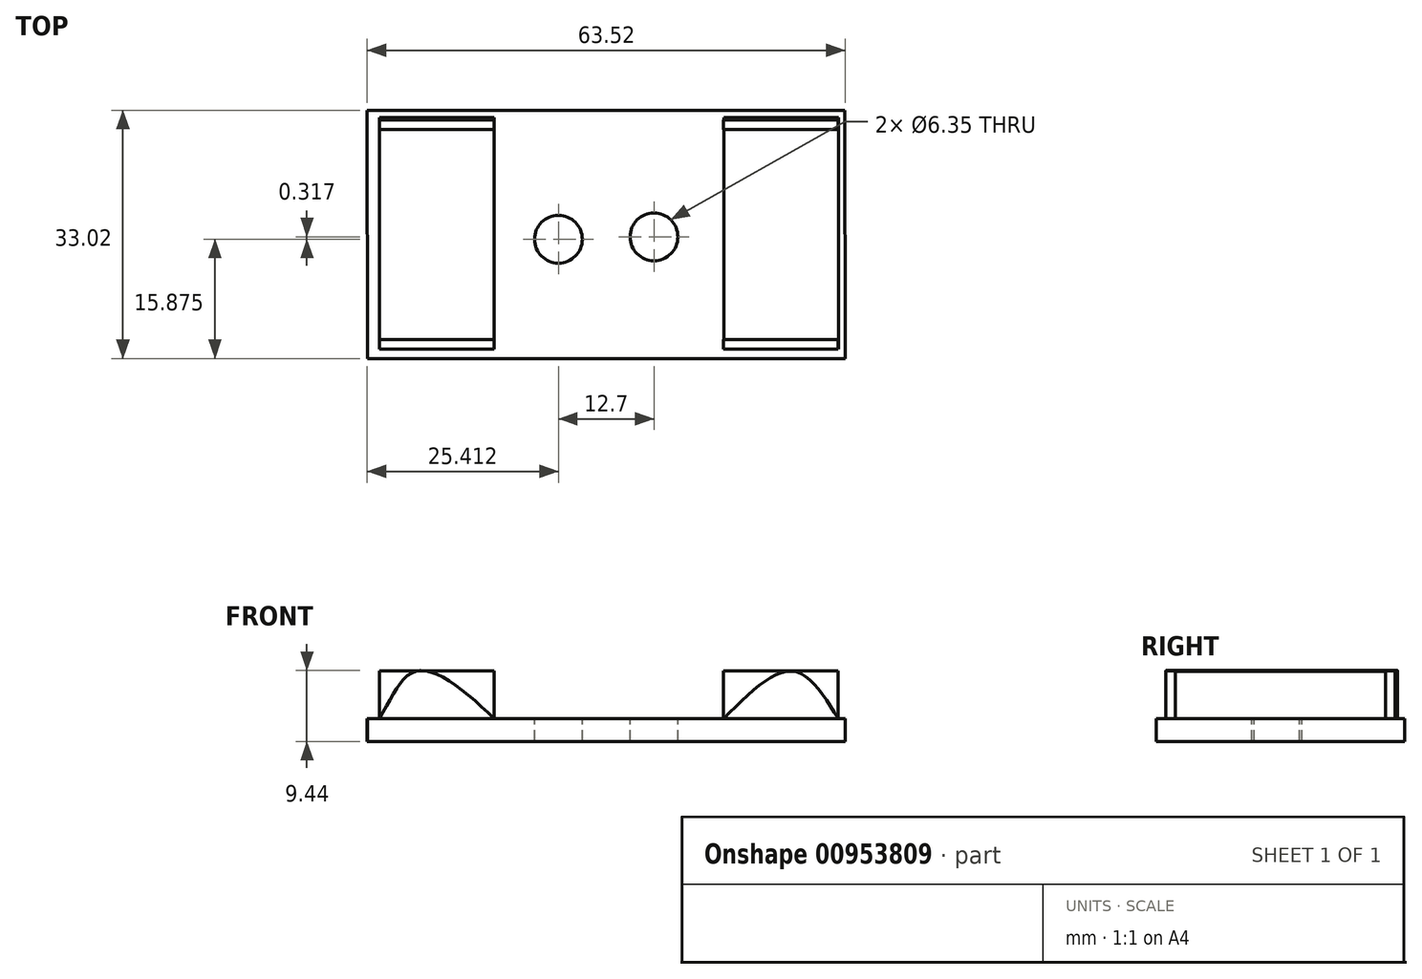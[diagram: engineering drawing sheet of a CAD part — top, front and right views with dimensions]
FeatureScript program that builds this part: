
annotation { "Feature Type Name" : "Feature", "Feature Type Description" : "" }
export const myFeature = defineFeature(function(context is Context, id is Id, definition is map)
    precondition{}
    {
        {
            var Q0;
            Q0=qCreatedBy(makeId("Top.planeOp"),FACE);
            var sketch = newSketch(context, id + "F0", { "sketchPlane" : qUnion([Q0])});
            skLineSegment(sketch, "E0", {"start": v(-16.83, 0) * mm, "end": v(46.67, 0) * mm});
            skLineSegment(sketch, "E1", {"start": v(46.67, 0) * mm, "end": v(46.65, 33.02) * mm});
            skLineSegment(sketch, "E2", {"start": v(46.65, 33.02) * mm, "end": v(-16.85, 33.02) * mm});
            skLineSegment(sketch, "E3", {"start": v(-16.85, 33.02) * mm, "end": v(-16.83, 0) * mm});
            skSolve(sketch);
        }
        {
            var Q0;
            Q0 = qSketchRegion(id + "F0", true);
            extrude(context, id + "F1", {"entities" : qUnion([Q0]), "depth" : 3.05 * mm, "offsetDistance" : 25.4 * mm});
        }
        {
            var Q0;
            Q0=makeQuery(id+"F1.opExtrude","CAP_FACE",FACE,{"disambiguationData":[OSD([sQuery(id+"F0.wireOp",EDGE,"E0"),sQuery(id+"F0.wireOp",EDGE,"E1"),sQuery(id+"F0.wireOp",EDGE,"E2"),sQuery(id+"F0.wireOp",EDGE,"E3")])],"isStart":false});
            var sketch = newSketch(context, id + "F2", { "sketchPlane" : qUnion([Q0])});
            skCircle(sketch, "E4", {"center": v(8.56, 15.88) * mm, "radius": 3.18 * mm});
            skCircle(sketch, "E5", {"center": v(21.26, 16.2) * mm, "radius": 3.18 * mm});
            skPoint(sketch, "E5.centerSnap0", {"position": v(-16.2, 16.2) * mm});
            skSolve(sketch);
        }
        {
            var Q0;
            Q0 = qSketchRegion(id + "F2", true);
            extrude(context, id + "F3", {"entities" : qUnion([Q0]), "operationType" : NewBodyOperationType.REMOVE, "endBound" : BoundingType.UP_TO_NEXT, "oppositeDirection" : true, "depth" : 3.05 * mm, "offsetDistance" : 25.4 * mm});
        }
        {
            var Q0;
            Q0=makeQuery(id+"F1.opExtrude","CAP_FACE",FACE,{"disambiguationData":[OSD([sQuery(id+"F0.wireOp",EDGE,"E0"),sQuery(id+"F0.wireOp",EDGE,"E1"),sQuery(id+"F0.wireOp",EDGE,"E2"),sQuery(id+"F0.wireOp",EDGE,"E3")])],"isStart":false});
            var sketch = newSketch(context, id + "F4", { "sketchPlane" : qUnion([Q0])});
            skLineSegment(sketch, "E6.bottom", {"start": v(-15.24, 31.75) * mm, "end": v(0, 31.75) * mm});
            skLineSegment(sketch, "E6.top", {"start": v(-15.24, 1.27) * mm, "end": v(0, 1.27) * mm});
            skLineSegment(sketch, "E6.left", {"start": v(-15.24, 31.75) * mm, "end": v(-15.24, 1.27) * mm});
            skLineSegment(sketch, "E6.right", {"start": v(0, 31.75) * mm, "end": v(0, 1.27) * mm});
            skLineSegment(sketch, "E7.bottom", {"start": v(30.52, 31.75) * mm, "end": v(45.76, 31.75) * mm});
            skLineSegment(sketch, "E7.top", {"start": v(30.52, 1.27) * mm, "end": v(45.76, 1.27) * mm});
            skLineSegment(sketch, "E7.left", {"start": v(30.52, 31.75) * mm, "end": v(30.52, 1.27) * mm});
            skLineSegment(sketch, "E7.right", {"start": v(45.76, 31.75) * mm, "end": v(45.76, 1.27) * mm});
            skSolve(sketch);
        }
        {
            var Q0;
            Q0 = qSketchRegion(id + "F4", true);
            extrude(context, id + "F5", {"entities" : qUnion([Q0]), "operationType" : NewBodyOperationType.ADD, "depth" : 6.35 * mm, "offsetDistance" : 25.4 * mm});
        }
        {
            var Q0;
            Q0=makeQuery(id+"F5.opExtrude","CAP_FACE",FACE,{"disambiguationData":[OSD([sQuery(id+"F4.wireOp",EDGE,"E6.bottom"),sQuery(id+"F4.wireOp",EDGE,"E6.top"),sQuery(id+"F4.wireOp",EDGE,"E6.left"),sQuery(id+"F4.wireOp",EDGE,"E6.right")])],"isStart":false});
            var sketch = newSketch(context, id + "F6", { "sketchPlane" : qUnion([Q0])});
            skLineSegment(sketch, "E8.bottom", {"start": v(-15.24, 30.48) * mm, "end": v(46.78, 30.48) * mm});
            skLineSegment(sketch, "E8.top", {"start": v(-15.24, 2.54) * mm, "end": v(46.78, 2.54) * mm});
            skLineSegment(sketch, "E8.left", {"start": v(-15.24, 30.48) * mm, "end": v(-15.24, 2.54) * mm});
            skLineSegment(sketch, "E8.right", {"start": v(46.78, 30.48) * mm, "end": v(46.78, 2.54) * mm});
            skSolve(sketch);
        }
        {
            var Q0;
            Q0 = qSketchRegion(id + "F6", true);
            extrude(context, id + "F7", {"entities" : qUnion([Q0]), "operationType" : NewBodyOperationType.REMOVE, "oppositeDirection" : true, "depth" : 6.35 * mm, "offsetDistance" : 25.4 * mm});
        }
        {
            var Q0;
            Q0=makeQuery(id+"F5.opExtrude","SWEPT_FACE",FACE,{"disambiguationData":[OSD([sQuery(id+"F4.wireOp",EDGE,"E6.top")])]});
            var sketch = newSketch(context, id + "F8", { "sketchPlane" : qUnion([Q0])});
            skFitSpline(sketch, "E9", {"points": [v(-15.24, 3.05) * mm, v(-10.16, 9.4) * mm, v(0, 3.05) * mm], "startDerivative": vector(11.3, 19.58) * mm, "endDerivative": vector(19, -18.7) * mm});
            skFitSpline(sketch, "E10", {"points": [v(-15.24, 3.05) * mm, v(0, 3.05) * mm], "startDerivative": vector(15.24, 0) * mm, "endDerivative": vector(15.24, 0) * mm});
            skFitSpline(sketch, "E11", {"points": [v(30.54, 3.06) * mm, v(39.67, 9.35) * mm, v(45.78, 3.07) * mm], "startDerivative": vector(18.36, 18.37) * mm, "endDerivative": vector(11.97, -18.95) * mm});
            skFitSpline(sketch, "E12", {"points": [v(45.78, 3.07) * mm, v(30.54, 3.06) * mm], "startDerivative": vector(-15.23, -0.1) * mm, "endDerivative": vector(-15.23, -0.1) * mm});
            skSolve(sketch);
        }
        {
            var Q0;
            Q0 = qSketchRegion(id + "F8", true);
            extrude(context, id + "F9", {"entities" : qUnion([Q0]), "oppositeDirection" : true, "depth" : 30.8 * mm, "offsetDistance" : 25.4 * mm});
        }
    });
